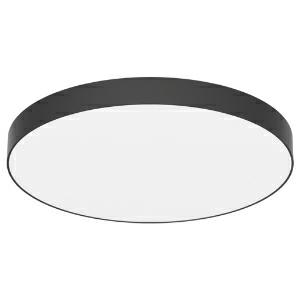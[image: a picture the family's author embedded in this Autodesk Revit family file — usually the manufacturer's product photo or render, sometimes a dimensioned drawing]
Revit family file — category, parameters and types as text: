
# Revit family: sign_opal_310-4010
name_source: partatom
category: Leuchten
revit_build: Autodesk Revit 2016 (Build: 20190508_0715(x64)
units: mm (PartAtom-declared; Revit-internal decimal feet)

## family parameters
Basisbauteil = Fläche
Beim Laden mit Abzugskörper schneiden = Nein
Bemaßung runder Anschluss = Durchmesser verwenden
Gemeinsam genutzt = Nein
Lichtquelle = Nein
Raumberechnungspunkt = Nein
Teiletyp = Normal

## types (1)
- 310-4010-D01-H30 (61 x LED, 436.43 lm, 3.1 W, 3000K)
    CIE Flux Codes = 47 78 95 100 75
    Color Rendering = 1B/80…89
    Color Temperature = 3000K
    Height = 120 mm
    Hersteller = Prolicht
    Lamp Light Flux = 436.43 lm
    Lamp Power = 3.1 W
    Lamp count = 61
    Lampe = 61 x LED
    Length = 1250 mm
    Luminous efficacy = 105 lm/W
    ModVariant = Nein
    Modell = 310-4010
    Mounting Place = Ceiling
    Mounting Type = Surface mounted
    Number of Poles = 1
    OnlyDefault = Ja
    Power Factor = 1
    Product Name = SIGN OPAL
    Product group = Surface lights
    ProductGroupID = 331
    Protection Class = Protection class
    Protection Degree = Degree of protection
    RLX_Detail_Level = 1
    RlxData = <blob elided: 29253 chars, md5=09d07cef>
    Scheinlast = 189 VA
    Socket = socket
    Standby Power = 0 W
    System Light Flux = 19887 lm
    System Power = 189 W
    Typenbild = 310-4010.jpg
    URL = http://relux.com
    VarID = 310-4010-d01-h30
    Voltage = 0 V
    Vorgabe-Ansicht = 1800 mm
    Weight = 0.00 kg
    Width = 0 mm  [stored 0 ft]

note: [stored X ft] marks values corroborated as IEEE doubles in the binary element streams (Revit-internal decimal feet)

## geometry (parser evidence)
native form markers: Blend x4, Sweep x13
no freeform markers — native parametric forms only
